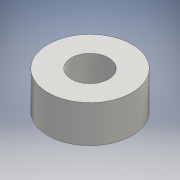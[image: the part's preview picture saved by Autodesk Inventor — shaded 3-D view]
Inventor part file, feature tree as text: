
AUTODESK INVENTOR PART (.ipt)
format: ipt  version: 2020.2 (Build 242310000, 310)  size: 93,696 bytes
history: native  units: mm
features: other x1, extrude x1, sketch x1
ambient origin geometry x8: Origin, YZ Plane, XZ Plane, XY Plane, X Axis, Y Axis, Z Axis, Center Point
bodies: Body1 (feature_tree)
feature tree (3):
  other  "ソリッド1"
  extrude  "押し出し1"  Depth=8.0mm
  sketch  "スケッチ1"
